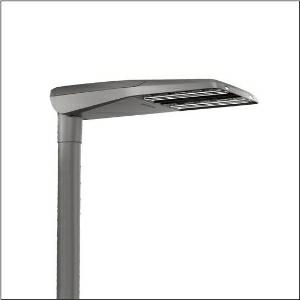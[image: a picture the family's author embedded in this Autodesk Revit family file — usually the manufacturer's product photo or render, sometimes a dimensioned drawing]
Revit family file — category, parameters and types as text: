
# Revit family: streetlight_sl_11_iq_midi___st1_2p1_0_5xc3g51e08me_ff57
name_source: partatom
category: Lighting Fixtures
units: mm (PartAtom-declared; Revit-internal decimal feet)

## family parameters
Cut with Voids When Loaded = No
Host = Face
Light Source = No
Part Type = Normal
Room Calculation Point = No
Round Connector Dimension = Use Diameter
Shared = No

## types (1)
- --- (1 x LED, 17750 lm, 124.7 W, 3000K)
    Apparent Load = 125 VA
    CIE Flux Codes = 31 68 95 100 100
    Color Rendering = 70
    Color Temperature = 3000K
    Default Elevation = 1800 mm
    Description = Streetlight SL 11 iQ midi, mast luminaire, primary light control with 3 zone facetted reflector, of plastic, silver coated, highly specular, primary optical cover: cover, of PMMA, transparent, light distribution: ST1.2P1.0, light emission: direct distribution, primary light characteristic: asymmetric, installation type: post-top, side-entry, LED, High Power LED, rated luminous flux: 17.750lm, luminous efficacy: 142lm/W, light colour: 730, colour temperature: 3000K, control: optimised constant luminous flux control (CLO 2.0), Desk-Remote (wireless, voltage-free reading and setting of iQ features in the workshop via application-optimized NFC function/RFID function), Light-Fading, Smart-Wire, Night-Set, Lumen-Switch, Temp-Guard, Auto-Match, with cable H07RN-F 5x 1.5mm², mains connection: 220..240V, AC, 50/60Hz, connection cable pre-assembled, cable length: 12,5m, start of lifetime: 125W, end of lifetime: 132W, reduction: 57W, luminaire housing, of diecast aluminium, powder-coated, Siteco® metallic grey (DB 702S), length: 780mm, width: 376mm, height: 118mm, spigot size: 60/76mm (post-top) and 42/60/76mm (side-entry), mast flange for spigot size: 42mm: 5XC10008XM4, 60mm: 5XC10008XM2, 76/60mm: 5XC10108XM1, equipment: Power, protection rating (complete): IP66, insulation class (complete): insulation class II (safety insulation), certification: CE, ENEC, VDE, impact resistance: IK09, permissible operating ambient temperature for outdoor applications: -25..+50°C, standard-compliant lighting for roads and squares, packaging unit: 1 piece

Light Distribution: ST1.2P1.0
    Height = 118 mm
    Lamp = 1 x LED
    Lamp Light Flux = 17750 lm
    Lamp Power = 124.7 W
    Lamp count = 1
    Length = 780 mm
    Luminous efficacy = 142 lm/W
    Manufacturer = Siteco
    ModVariant = No
    Model = 5XC3G51E08ME
    Number of Poles = 1
    OnlyDefault = Yes
    Power Factor = 1
    Product Name = Streetlight SL 11 iQ midi | ST1.2P1.0
    Product group = mast luminaire | pylon top
    ProductGroupID = 6100
    Protection Class = Protection class II
    Protection Degree = IP 66
    RLX_Detail_Level = 1
    RlxData = <blob elided: 70361 chars, md5=ac39c2d1>
    Socket = socket
    Standby Power = 0 W
    System Light Flux = 17750 lm
    System Power = 125 W
    Type Comments = factory setting: luminous flux: 100 % | dim-lin: 254 | 557 mA
    Type Image = l_1005960.jpg
    URL = http://relux.com
    VarID = @adj_116171
    Voltage = 0 V
    Weight = 0.00 kg
    Width = 376 mm

## geometry (parser evidence)
native form markers: Blend x4, Sweep x9
no freeform markers — native parametric forms only
